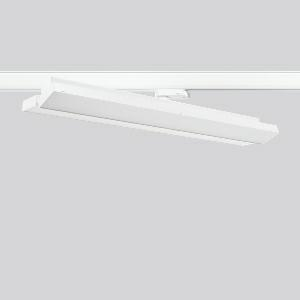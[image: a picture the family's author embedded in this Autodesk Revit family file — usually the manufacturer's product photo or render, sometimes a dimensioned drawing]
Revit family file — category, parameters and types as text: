
# Revit family: tx-move_742164_002_76_88cd
name_source: partatom
category: Lighting Fixtures
units: mm (PartAtom-declared; Revit-internal decimal feet)

## family parameters
Cut with Voids When Loaded = No
Host = Face
Light Source = No
Part Type = Normal
Room Calculation Point = No
Round Connector Dimension = Use Diameter
Shared = No

## types (1)
- MultiLumen 1 (1 x LED Modul 830, 2450 lm, 3000)
    Apparent Load = 41 VA
    CIE Flux Codes = 47 79 96 100 100
    Color Rendering = 80
    Color Temperature = 3000
    Default Elevation = 1800 mm
    Description = Series: TX-MOVE
Multifunctional surface-mounted spotlight for area lighting. Very flat design. Housing: sheet steel, powder-coated. Rotation range: 356°. Swivel range: 90°. Consistent alignment possible with visible tilt scale. High-efficiency LED units with flush-mounted opal diffuser made of non-yellowing PMMA. Symmetrical wide beam light emission. With adapter for RZB 3-circuit DALI tracks. Suitable for Track on ceiling. MultiLumen: Luminous flux adjustable in 3 steps. Factory setting is the highest luminous flux. Environmentally friendly and resource-saving due to replaceable and recyclable components. 
Colour: traffic white, matt (RAL 9016)
Length: 570 mm
Width: 119 mm
Height: 88 mm
Lamp: LED
Socket: without socket
Colour temperature: 3000K
Colour rendering index (CRI): 80
System power: 41 W
Rated luminous flux: 4900 lm
Luminous efficiency: 120 lm/W
System power 2: 57 W
Rated luminous flux 2: 6650 lm
Luminous efficiency 2: 117 lm/W
System power 3: 73 W
Rated luminous flux 3: 8150 lm
Luminous efficiency 3: 112 lm/W
Control gear: Dimmable EVG, DALI
Protection class: I
Type of protection: IP 20
    Height = 75 mm
    Lamp = 1 x LED Modul 830
    Lamp Light Flux = 2450 lm
    Lamp count = 1
    Length = 569 mm
    Lifetime = 50000 h
    Luminous efficacy = 120 lm/W
    Manufacturer = RZB
    ModVariant = No
    Model = 742164.002.76
    Mounting Place = Ceiling
    Mounting Type = Surface mounted
    Number of Poles = 1
    OnlyDefault = Yes
    Power Factor = 1
    Product Name = TX-MOVE
    Product group = Track mounted projectors
    ProductGroupID = 301
    Protection Class = Protection class I
    Protection Degree = IP 20
    RLX_Detail_Level = 1
    RLX_Emergency_Light_Flux = 0 lm
    RLX_Emergency_Type = 0
    RLX_Emergency_Type_DB = No
    RlxData = <blob elided: 29869 chars, md5=d25c5977>
    Socket = socket
    Standby Power = 0 W
    System Light Flux = 4900 lm
    System Power = 41 W
    Type Comments = MultiLumen 1
    Type Image = 742164.002.jpg
    URL = http://relux.com
    VarID = multilumen_1
    Voltage = 0 V
    Weight = 0.00 kg
    Width = 119 mm

## geometry (parser evidence)
native form markers: Blend x4, Sweep x15
no freeform markers — native parametric forms only
